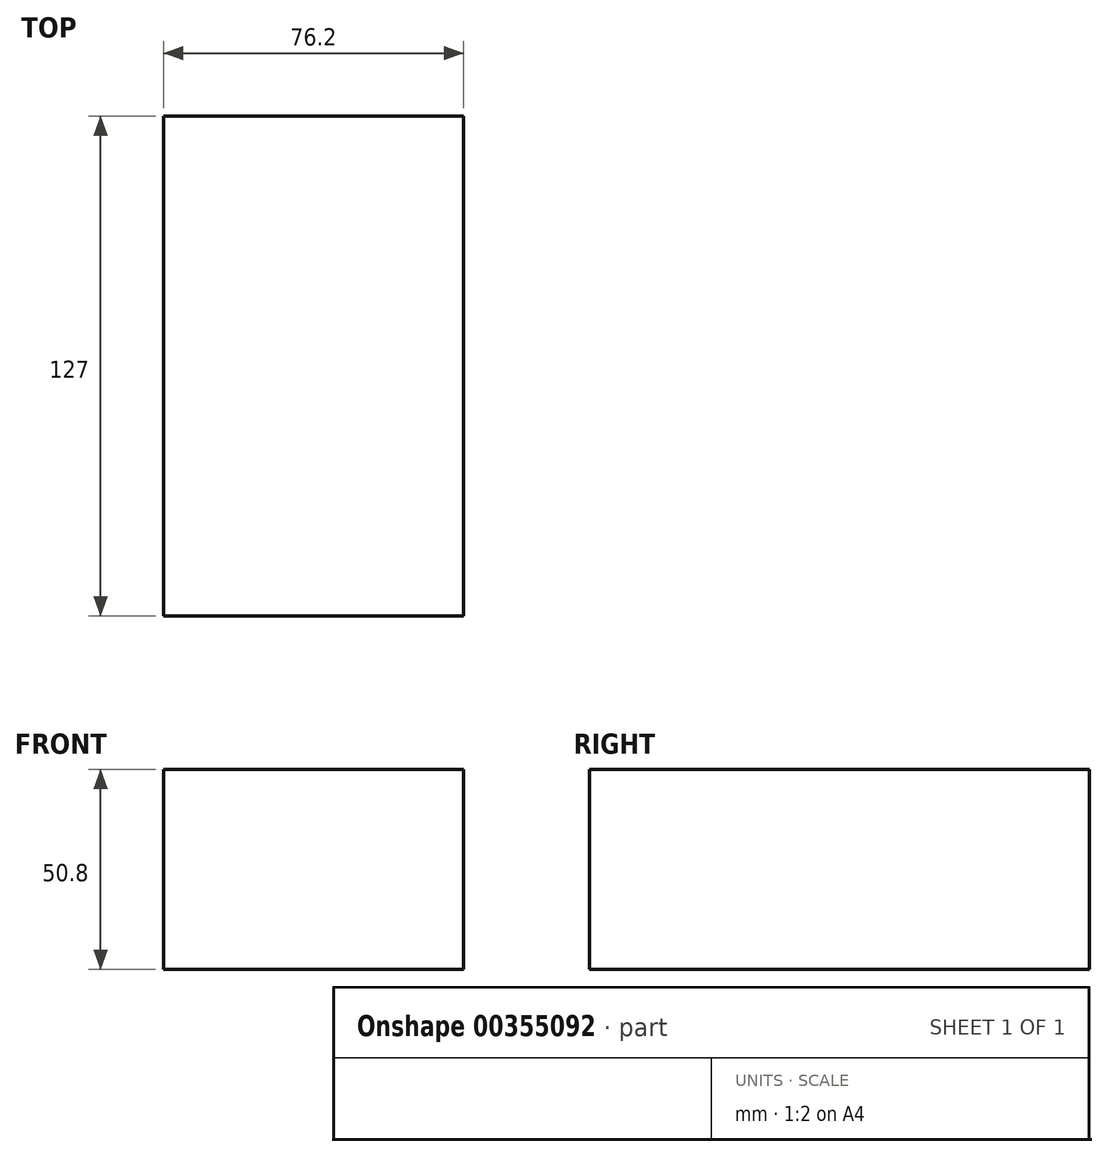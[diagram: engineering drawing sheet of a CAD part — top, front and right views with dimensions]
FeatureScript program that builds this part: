
annotation { "Feature Type Name" : "Feature", "Feature Type Description" : "" }
export const myFeature = defineFeature(function(context is Context, id is Id, definition is map)
    precondition{}
    {
        {
            var Q0;
            Q0=qCreatedBy(makeId("Front.planeOp"),FACE);
            var sketch = newSketch(context, id + "F0", { "sketchPlane" : qUnion([Q0])});
            skLineSegment(sketch, "E0.bottom", {"start": v(0, 0) * mm, "end": v(-76.2, 0) * mm});
            skLineSegment(sketch, "E0.top", {"start": v(0, 50.8) * mm, "end": v(-76.2, 50.8) * mm});
            skLineSegment(sketch, "E0.left", {"start": v(0, 0) * mm, "end": v(0, 50.8) * mm});
            skLineSegment(sketch, "E0.right", {"start": v(-76.2, 0) * mm, "end": v(-76.2, 50.8) * mm});
            skSolve(sketch);
        }
        {
            var Q0;
            Q0=makeQuery(id+"F0.imprint","IMPRINT",FACE,{"disambiguationData":[TD([[makeQuery(id+"F0.imprint","IMPRINT",EDGE,{"derivedFrom":sQuery(id+"F0.wireOp",EDGE,"E0.bottom")}),-1.0]])]});
            extrude(context, id + "F1", {"entities" : qUnion([Q0]), "depth" : 127 * mm});
        }
    });
